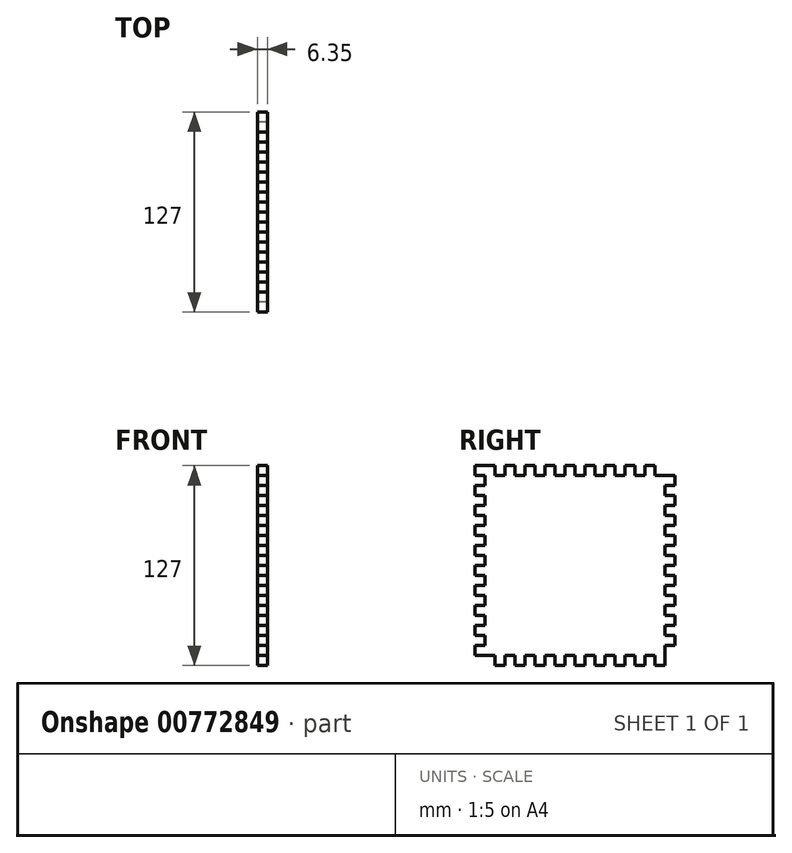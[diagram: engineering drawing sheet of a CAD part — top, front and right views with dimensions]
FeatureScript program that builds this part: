
annotation { "Feature Type Name" : "Feature", "Feature Type Description" : "" }
export const myFeature = defineFeature(function(context is Context, id is Id, definition is map)
    precondition{}
    {
        {
            var Q0;
            Q0=qCreatedBy(makeId("Right.planeOp"),FACE);
            var sketch = newSketch(context, id + "F0", { "sketchPlane" : qUnion([Q0])});
            skLineSegment(sketch, "E0.top", {"start": v(6.35, 127) * mm, "end": v(12.7, 127) * mm});
            skLineSegment(sketch, "E1.top", {"start": v(0, 120.65) * mm, "end": v(6.35, 120.65) * mm});
            skLineSegment(sketch, "E2.1.0.0", {"start": v(12.7, 127) * mm, "end": v(12.7, 120.65) * mm});
            skLineSegment(sketch, "E2.2.0.0", {"start": v(19.05, 127) * mm, "end": v(19.05, 120.65) * mm});
            skLineSegment(sketch, "E2.2.0.1", {"start": v(12.7, 120.65) * mm, "end": v(19.05, 120.65) * mm});
            skLineSegment(sketch, "E2.2.0.2", {"start": v(12.7, 127) * mm, "end": v(12.7, 120.65) * mm});
            skLineSegment(sketch, "E2.3.0.0", {"start": v(25.4, 127) * mm, "end": v(25.4, 120.65) * mm});
            skLineSegment(sketch, "E2.3.0.2", {"start": v(19.05, 127) * mm, "end": v(19.05, 120.65) * mm});
            skLineSegment(sketch, "E2.4.0.0", {"start": v(31.75, 127) * mm, "end": v(31.75, 120.65) * mm});
            skLineSegment(sketch, "E2.4.0.1", {"start": v(25.4, 120.65) * mm, "end": v(31.75, 120.65) * mm});
            skLineSegment(sketch, "E2.4.0.2", {"start": v(25.4, 127) * mm, "end": v(25.4, 120.65) * mm});
            skLineSegment(sketch, "E2.5.0.0", {"start": v(38.1, 127) * mm, "end": v(38.1, 120.65) * mm});
            skLineSegment(sketch, "E2.5.0.2", {"start": v(31.75, 127) * mm, "end": v(31.75, 120.65) * mm});
            skLineSegment(sketch, "E2.6.0.0", {"start": v(44.45, 127) * mm, "end": v(44.45, 120.65) * mm});
            skLineSegment(sketch, "E2.6.0.1", {"start": v(38.1, 120.65) * mm, "end": v(44.45, 120.65) * mm});
            skLineSegment(sketch, "E2.6.0.2", {"start": v(38.1, 127) * mm, "end": v(38.1, 120.65) * mm});
            skLineSegment(sketch, "E2.7.0.0", {"start": v(50.8, 127) * mm, "end": v(50.8, 120.65) * mm});
            skLineSegment(sketch, "E2.7.0.2", {"start": v(44.45, 127) * mm, "end": v(44.45, 120.65) * mm});
            skLineSegment(sketch, "E2.8.0.0", {"start": v(57.15, 127) * mm, "end": v(57.15, 120.65) * mm});
            skLineSegment(sketch, "E2.8.0.1", {"start": v(50.8, 120.65) * mm, "end": v(57.15, 120.65) * mm});
            skLineSegment(sketch, "E2.8.0.2", {"start": v(50.8, 127) * mm, "end": v(50.8, 120.65) * mm});
            skLineSegment(sketch, "E2.9.0.0", {"start": v(63.5, 127) * mm, "end": v(63.5, 120.65) * mm});
            skLineSegment(sketch, "E2.9.0.2", {"start": v(57.15, 127) * mm, "end": v(57.15, 120.65) * mm});
            skLineSegment(sketch, "E2.10.0.0", {"start": v(69.85, 127) * mm, "end": v(69.85, 120.65) * mm});
            skLineSegment(sketch, "E2.10.0.1", {"start": v(63.5, 120.65) * mm, "end": v(69.85, 120.65) * mm});
            skLineSegment(sketch, "E2.10.0.2", {"start": v(63.5, 127) * mm, "end": v(63.5, 120.65) * mm});
            skLineSegment(sketch, "E2.11.0.0", {"start": v(76.2, 127) * mm, "end": v(76.2, 120.65) * mm});
            skLineSegment(sketch, "E2.11.0.2", {"start": v(69.85, 127) * mm, "end": v(69.85, 120.65) * mm});
            skLineSegment(sketch, "E2.12.0.0", {"start": v(82.55, 127) * mm, "end": v(82.55, 120.65) * mm});
            skLineSegment(sketch, "E2.12.0.1", {"start": v(76.2, 120.65) * mm, "end": v(82.55, 120.65) * mm});
            skLineSegment(sketch, "E2.12.0.2", {"start": v(76.2, 127) * mm, "end": v(76.2, 120.65) * mm});
            skLineSegment(sketch, "E2.13.0.0", {"start": v(88.9, 127) * mm, "end": v(88.9, 120.65) * mm});
            skLineSegment(sketch, "E2.13.0.2", {"start": v(82.55, 127) * mm, "end": v(82.55, 120.65) * mm});
            skLineSegment(sketch, "E2.14.0.0", {"start": v(95.25, 127) * mm, "end": v(95.25, 120.65) * mm});
            skLineSegment(sketch, "E2.14.0.1", {"start": v(88.9, 120.65) * mm, "end": v(95.25, 120.65) * mm});
            skLineSegment(sketch, "E2.14.0.2", {"start": v(88.9, 127) * mm, "end": v(88.9, 120.65) * mm});
            skLineSegment(sketch, "E2.15.0.0", {"start": v(101.6, 127) * mm, "end": v(101.6, 120.65) * mm});
            skLineSegment(sketch, "E2.15.0.2", {"start": v(95.25, 127) * mm, "end": v(95.25, 120.65) * mm});
            skLineSegment(sketch, "E2.16.0.0", {"start": v(107.95, 127) * mm, "end": v(107.95, 120.65) * mm});
            skLineSegment(sketch, "E2.16.0.1", {"start": v(101.6, 120.65) * mm, "end": v(107.95, 120.65) * mm});
            skLineSegment(sketch, "E2.16.0.2", {"start": v(101.6, 127) * mm, "end": v(101.6, 120.65) * mm});
            skLineSegment(sketch, "E2.17.0.0", {"start": v(114.3, 127) * mm, "end": v(114.3, 120.65) * mm});
            skLineSegment(sketch, "E2.17.0.2", {"start": v(107.95, 127) * mm, "end": v(107.95, 120.65) * mm});
            skLineSegment(sketch, "E2.18.0.1", {"start": v(114.3, 120.65) * mm, "end": v(120.65, 120.65) * mm});
            skLineSegment(sketch, "E2.18.0.2", {"start": v(114.3, 127) * mm, "end": v(114.3, 120.65) * mm});
            skLineSegment(sketch, "E3.trimOffspring", {"start": v(19.05, 127) * mm, "end": v(25.4, 127) * mm});
            skLineSegment(sketch, "E4.trimOffspring", {"start": v(31.75, 127) * mm, "end": v(38.1, 127) * mm});
            skLineSegment(sketch, "E5.trimOffspring", {"start": v(44.45, 127) * mm, "end": v(50.8, 127) * mm});
            skLineSegment(sketch, "E6.trimOffspring", {"start": v(57.15, 127) * mm, "end": v(63.5, 127) * mm});
            skLineSegment(sketch, "E7.trimOffspring", {"start": v(69.85, 127) * mm, "end": v(76.2, 127) * mm});
            skLineSegment(sketch, "E8.trimOffspring", {"start": v(82.55, 127) * mm, "end": v(88.9, 127) * mm});
            skLineSegment(sketch, "E9.trimOffspring", {"start": v(95.25, 127) * mm, "end": v(101.6, 127) * mm});
            skLineSegment(sketch, "E10.trimOffspring", {"start": v(107.95, 127) * mm, "end": v(114.3, 127) * mm});
            skLineSegment(sketch, "E11.0.1.1", {"start": v(120.65, 114.3) * mm, "end": v(127, 114.3) * mm});
            skLineSegment(sketch, "E11.0.1.2", {"start": v(127, 120.65) * mm, "end": v(127, 114.3) * mm});
            skLineSegment(sketch, "E11.0.2.0", {"start": v(120.65, 114.3) * mm, "end": v(127, 114.3) * mm});
            skLineSegment(sketch, "E11.0.2.1", {"start": v(120.65, 107.95) * mm, "end": v(127, 107.95) * mm});
            skLineSegment(sketch, "E11.0.2.3", {"start": v(120.65, 114.3) * mm, "end": v(120.65, 107.95) * mm});
            skLineSegment(sketch, "E11.0.3.0", {"start": v(120.65, 107.95) * mm, "end": v(127, 107.95) * mm});
            skLineSegment(sketch, "E11.0.3.1", {"start": v(120.65, 101.6) * mm, "end": v(127, 101.6) * mm});
            skLineSegment(sketch, "E11.0.3.2", {"start": v(127, 107.95) * mm, "end": v(127, 101.6) * mm});
            skLineSegment(sketch, "E11.0.4.0", {"start": v(120.65, 101.6) * mm, "end": v(127, 101.6) * mm});
            skLineSegment(sketch, "E11.0.4.1", {"start": v(120.65, 95.25) * mm, "end": v(127, 95.25) * mm});
            skLineSegment(sketch, "E11.0.4.3", {"start": v(120.65, 101.6) * mm, "end": v(120.65, 95.25) * mm});
            skLineSegment(sketch, "E11.0.5.0", {"start": v(120.65, 95.25) * mm, "end": v(127, 95.25) * mm});
            skLineSegment(sketch, "E11.0.5.1", {"start": v(120.65, 88.9) * mm, "end": v(127, 88.9) * mm});
            skLineSegment(sketch, "E11.0.6.0", {"start": v(120.65, 88.9) * mm, "end": v(127, 88.9) * mm});
            skLineSegment(sketch, "E11.0.6.1", {"start": v(120.65, 82.55) * mm, "end": v(127, 82.55) * mm});
            skLineSegment(sketch, "E11.0.6.3", {"start": v(120.65, 88.9) * mm, "end": v(120.65, 82.55) * mm});
            skLineSegment(sketch, "E11.0.7.0", {"start": v(120.65, 82.55) * mm, "end": v(127, 82.55) * mm});
            skLineSegment(sketch, "E11.0.7.1", {"start": v(120.65, 76.2) * mm, "end": v(127, 76.2) * mm});
            skLineSegment(sketch, "E11.0.8.0", {"start": v(120.65, 76.2) * mm, "end": v(127, 76.2) * mm});
            skLineSegment(sketch, "E11.0.8.1", {"start": v(120.65, 69.85) * mm, "end": v(127, 69.85) * mm});
            skLineSegment(sketch, "E11.0.8.3", {"start": v(120.65, 76.2) * mm, "end": v(120.65, 69.85) * mm});
            skLineSegment(sketch, "E11.0.9.0", {"start": v(120.65, 69.85) * mm, "end": v(127, 69.85) * mm});
            skLineSegment(sketch, "E11.0.9.1", {"start": v(120.65, 63.5) * mm, "end": v(127, 63.5) * mm});
            skLineSegment(sketch, "E11.0.10.0", {"start": v(120.65, 63.5) * mm, "end": v(127, 63.5) * mm});
            skLineSegment(sketch, "E11.0.10.1", {"start": v(120.65, 57.15) * mm, "end": v(127, 57.15) * mm});
            skLineSegment(sketch, "E11.0.10.3", {"start": v(120.65, 63.5) * mm, "end": v(120.65, 57.15) * mm});
            skLineSegment(sketch, "E11.0.11.0", {"start": v(120.65, 57.15) * mm, "end": v(127, 57.15) * mm});
            skLineSegment(sketch, "E11.0.11.1", {"start": v(120.65, 50.8) * mm, "end": v(127, 50.8) * mm});
            skLineSegment(sketch, "E11.0.12.0", {"start": v(120.65, 50.8) * mm, "end": v(127, 50.8) * mm});
            skLineSegment(sketch, "E11.0.12.1", {"start": v(120.65, 44.45) * mm, "end": v(127, 44.45) * mm});
            skLineSegment(sketch, "E11.0.12.3", {"start": v(120.65, 50.8) * mm, "end": v(120.65, 44.45) * mm});
            skLineSegment(sketch, "E11.0.13.0", {"start": v(120.65, 44.45) * mm, "end": v(127, 44.45) * mm});
            skLineSegment(sketch, "E11.0.13.1", {"start": v(120.65, 38.1) * mm, "end": v(127, 38.1) * mm});
            skLineSegment(sketch, "E11.0.14.0", {"start": v(120.65, 38.1) * mm, "end": v(127, 38.1) * mm});
            skLineSegment(sketch, "E11.0.14.1", {"start": v(120.65, 31.75) * mm, "end": v(127, 31.75) * mm});
            skLineSegment(sketch, "E11.0.14.3", {"start": v(120.65, 38.1) * mm, "end": v(120.65, 31.75) * mm});
            skLineSegment(sketch, "E11.0.15.0", {"start": v(120.65, 31.75) * mm, "end": v(127, 31.75) * mm});
            skLineSegment(sketch, "E11.0.15.1", {"start": v(120.65, 25.4) * mm, "end": v(127, 25.4) * mm});
            skLineSegment(sketch, "E11.0.16.0", {"start": v(120.65, 25.4) * mm, "end": v(127, 25.4) * mm});
            skLineSegment(sketch, "E11.0.16.1", {"start": v(120.65, 19.05) * mm, "end": v(127, 19.05) * mm});
            skLineSegment(sketch, "E11.0.16.3", {"start": v(120.65, 25.4) * mm, "end": v(120.65, 19.05) * mm});
            skLineSegment(sketch, "E11.0.17.0", {"start": v(120.65, 19.05) * mm, "end": v(127, 19.05) * mm});
            skLineSegment(sketch, "E11.0.17.1", {"start": v(120.65, 12.7) * mm, "end": v(127, 12.7) * mm});
            skLineSegment(sketch, "E11.0.17.2", {"start": v(127, 19.05) * mm, "end": v(127, 12.7) * mm});
            skLineSegment(sketch, "E11.0.18.0", {"start": v(120.65, 12.7) * mm, "end": v(127, 12.7) * mm});
            skLineSegment(sketch, "E11.0.18.3", {"start": v(120.65, 12.7) * mm, "end": v(120.65, 6.35) * mm});
            skLineSegment(sketch, "E12.trimOffspring", {"start": v(127, 88.9) * mm, "end": v(127, 95.25) * mm});
            skLineSegment(sketch, "E13.trimOffspring", {"start": v(127, 76.2) * mm, "end": v(127, 82.55) * mm});
            skLineSegment(sketch, "E14.trimOffspring", {"start": v(127, 63.5) * mm, "end": v(127, 69.85) * mm});
            skLineSegment(sketch, "E15.trimOffspring", {"start": v(127, 50.8) * mm, "end": v(127, 57.15) * mm});
            skLineSegment(sketch, "E16.trimOffspring", {"start": v(127, 38.1) * mm, "end": v(127, 44.45) * mm});
            skLineSegment(sketch, "E17.trimOffspring", {"start": v(127, 25.4) * mm, "end": v(127, 31.75) * mm});
            skLineSegment(sketch, "E18.trimOffspring", {"start": v(127, 12.7) * mm, "end": v(127, 19.05) * mm});
            skLineSegment(sketch, "E19.1.0.0", {"start": v(114.3, 0) * mm, "end": v(114.3, 6.35) * mm});
            skLineSegment(sketch, "E19.1.0.3", {"start": v(114.3, 0) * mm, "end": v(120.65, 0) * mm});
            skLineSegment(sketch, "E19.2.0.0", {"start": v(107.95, 0) * mm, "end": v(107.95, 6.35) * mm});
            skLineSegment(sketch, "E19.2.0.1", {"start": v(114.3, 6.35) * mm, "end": v(107.95, 6.35) * mm});
            skLineSegment(sketch, "E19.2.0.2", {"start": v(114.3, 0) * mm, "end": v(114.3, 6.35) * mm});
            skLineSegment(sketch, "E19.3.0.0", {"start": v(101.6, 0) * mm, "end": v(101.6, 6.35) * mm});
            skLineSegment(sketch, "E19.3.0.2", {"start": v(107.95, 0) * mm, "end": v(107.95, 6.35) * mm});
            skLineSegment(sketch, "E19.3.0.3", {"start": v(101.6, 0) * mm, "end": v(107.95, 0) * mm});
            skLineSegment(sketch, "E19.4.0.0", {"start": v(95.25, 0) * mm, "end": v(95.25, 6.35) * mm});
            skLineSegment(sketch, "E19.4.0.1", {"start": v(101.6, 6.35) * mm, "end": v(95.25, 6.35) * mm});
            skLineSegment(sketch, "E19.4.0.2", {"start": v(101.6, 0) * mm, "end": v(101.6, 6.35) * mm});
            skLineSegment(sketch, "E19.5.0.0", {"start": v(88.9, 0) * mm, "end": v(88.9, 6.35) * mm});
            skLineSegment(sketch, "E19.5.0.2", {"start": v(95.25, 0) * mm, "end": v(95.25, 6.35) * mm});
            skLineSegment(sketch, "E19.5.0.3", {"start": v(88.9, 0) * mm, "end": v(95.25, 0) * mm});
            skLineSegment(sketch, "E19.6.0.0", {"start": v(82.55, 0) * mm, "end": v(82.55, 6.35) * mm});
            skLineSegment(sketch, "E19.6.0.1", {"start": v(88.9, 6.35) * mm, "end": v(82.55, 6.35) * mm});
            skLineSegment(sketch, "E19.6.0.2", {"start": v(88.9, 0) * mm, "end": v(88.9, 6.35) * mm});
            skLineSegment(sketch, "E19.7.0.0", {"start": v(76.2, 0) * mm, "end": v(76.2, 6.35) * mm});
            skLineSegment(sketch, "E19.7.0.2", {"start": v(82.55, 0) * mm, "end": v(82.55, 6.35) * mm});
            skLineSegment(sketch, "E19.7.0.3", {"start": v(76.2, 0) * mm, "end": v(82.55, 0) * mm});
            skLineSegment(sketch, "E19.8.0.0", {"start": v(69.85, 0) * mm, "end": v(69.85, 6.35) * mm});
            skLineSegment(sketch, "E19.8.0.1", {"start": v(76.2, 6.35) * mm, "end": v(69.85, 6.35) * mm});
            skLineSegment(sketch, "E19.8.0.2", {"start": v(76.2, 0) * mm, "end": v(76.2, 6.35) * mm});
            skLineSegment(sketch, "E19.9.0.0", {"start": v(63.5, 0) * mm, "end": v(63.5, 6.35) * mm});
            skLineSegment(sketch, "E19.9.0.2", {"start": v(69.85, 0) * mm, "end": v(69.85, 6.35) * mm});
            skLineSegment(sketch, "E19.9.0.3", {"start": v(63.5, 0) * mm, "end": v(69.85, 0) * mm});
            skLineSegment(sketch, "E19.10.0.0", {"start": v(57.15, 0) * mm, "end": v(57.15, 6.35) * mm});
            skLineSegment(sketch, "E19.10.0.1", {"start": v(63.5, 6.35) * mm, "end": v(57.15, 6.35) * mm});
            skLineSegment(sketch, "E19.10.0.2", {"start": v(63.5, 0) * mm, "end": v(63.5, 6.35) * mm});
            skLineSegment(sketch, "E19.11.0.0", {"start": v(50.8, 0) * mm, "end": v(50.8, 6.35) * mm});
            skLineSegment(sketch, "E19.11.0.2", {"start": v(57.15, 0) * mm, "end": v(57.15, 6.35) * mm});
            skLineSegment(sketch, "E19.11.0.3", {"start": v(50.8, 0) * mm, "end": v(57.15, 0) * mm});
            skLineSegment(sketch, "E19.12.0.0", {"start": v(44.45, 0) * mm, "end": v(44.45, 6.35) * mm});
            skLineSegment(sketch, "E19.12.0.1", {"start": v(50.8, 6.35) * mm, "end": v(44.45, 6.35) * mm});
            skLineSegment(sketch, "E19.12.0.2", {"start": v(50.8, 0) * mm, "end": v(50.8, 6.35) * mm});
            skLineSegment(sketch, "E19.13.0.0", {"start": v(38.1, 0) * mm, "end": v(38.1, 6.35) * mm});
            skLineSegment(sketch, "E19.13.0.2", {"start": v(44.45, 0) * mm, "end": v(44.45, 6.35) * mm});
            skLineSegment(sketch, "E19.13.0.3", {"start": v(38.1, 0) * mm, "end": v(44.45, 0) * mm});
            skLineSegment(sketch, "E19.14.0.0", {"start": v(31.75, 0) * mm, "end": v(31.75, 6.35) * mm});
            skLineSegment(sketch, "E19.14.0.1", {"start": v(38.1, 6.35) * mm, "end": v(31.75, 6.35) * mm});
            skLineSegment(sketch, "E19.14.0.2", {"start": v(38.1, 0) * mm, "end": v(38.1, 6.35) * mm});
            skLineSegment(sketch, "E19.15.0.0", {"start": v(25.4, 0) * mm, "end": v(25.4, 6.35) * mm});
            skLineSegment(sketch, "E19.15.0.2", {"start": v(31.75, 0) * mm, "end": v(31.75, 6.35) * mm});
            skLineSegment(sketch, "E19.15.0.3", {"start": v(25.4, 0) * mm, "end": v(31.75, 0) * mm});
            skLineSegment(sketch, "E19.16.0.0", {"start": v(19.05, 0) * mm, "end": v(19.05, 6.35) * mm});
            skLineSegment(sketch, "E19.16.0.1", {"start": v(25.4, 6.35) * mm, "end": v(19.05, 6.35) * mm});
            skLineSegment(sketch, "E19.16.0.2", {"start": v(25.4, 0) * mm, "end": v(25.4, 6.35) * mm});
            skLineSegment(sketch, "E19.17.0.0", {"start": v(12.7, 0) * mm, "end": v(12.7, 6.35) * mm});
            skLineSegment(sketch, "E19.17.0.2", {"start": v(19.05, 0) * mm, "end": v(19.05, 6.35) * mm});
            skLineSegment(sketch, "E19.17.0.3", {"start": v(12.7, 0) * mm, "end": v(19.05, 0) * mm});
            skLineSegment(sketch, "E19.18.0.1", {"start": v(12.7, 6.35) * mm, "end": v(6.35, 6.35) * mm});
            skLineSegment(sketch, "E19.18.0.2", {"start": v(12.7, 0) * mm, "end": v(12.7, 6.35) * mm});
            skLineSegment(sketch, "E19.direction1", {"start": v(120.65, 0) * mm, "end": v(114.3, 0) * mm, "construction": true});
            skLineSegment(sketch, "E20.0.1.0", {"start": v(6.35, 12.7) * mm, "end": v(0, 12.7) * mm});
            skLineSegment(sketch, "E20.0.1.1", {"start": v(0, 6.35) * mm, "end": v(0, 12.7) * mm});
            skLineSegment(sketch, "E20.0.2.0", {"start": v(6.35, 19.05) * mm, "end": v(0, 19.05) * mm});
            skLineSegment(sketch, "E20.0.2.2", {"start": v(0, 12.7) * mm, "end": v(6.35, 12.7) * mm});
            skLineSegment(sketch, "E20.0.2.3", {"start": v(6.35, 12.7) * mm, "end": v(6.35, 19.05) * mm});
            skLineSegment(sketch, "E20.0.3.0", {"start": v(6.35, 25.4) * mm, "end": v(0, 25.4) * mm});
            skLineSegment(sketch, "E20.0.3.1", {"start": v(0, 19.05) * mm, "end": v(0, 25.4) * mm});
            skLineSegment(sketch, "E20.0.3.2", {"start": v(0, 19.05) * mm, "end": v(6.35, 19.05) * mm});
            skLineSegment(sketch, "E20.0.4.0", {"start": v(6.35, 31.75) * mm, "end": v(0, 31.75) * mm});
            skLineSegment(sketch, "E20.0.4.2", {"start": v(0, 25.4) * mm, "end": v(6.35, 25.4) * mm});
            skLineSegment(sketch, "E20.0.4.3", {"start": v(6.35, 25.4) * mm, "end": v(6.35, 31.75) * mm});
            skLineSegment(sketch, "E20.0.5.0", {"start": v(6.35, 38.1) * mm, "end": v(0, 38.1) * mm});
            skLineSegment(sketch, "E20.0.5.1", {"start": v(0, 31.75) * mm, "end": v(0, 38.1) * mm});
            skLineSegment(sketch, "E20.0.5.2", {"start": v(0, 31.75) * mm, "end": v(6.35, 31.75) * mm});
            skLineSegment(sketch, "E20.0.6.0", {"start": v(6.35, 44.45) * mm, "end": v(0, 44.45) * mm});
            skLineSegment(sketch, "E20.0.6.2", {"start": v(0, 38.1) * mm, "end": v(6.35, 38.1) * mm});
            skLineSegment(sketch, "E20.0.6.3", {"start": v(6.35, 38.1) * mm, "end": v(6.35, 44.45) * mm});
            skLineSegment(sketch, "E20.0.7.0", {"start": v(6.35, 50.8) * mm, "end": v(0, 50.8) * mm});
            skLineSegment(sketch, "E20.0.7.1", {"start": v(0, 44.45) * mm, "end": v(0, 50.8) * mm});
            skLineSegment(sketch, "E20.0.7.2", {"start": v(0, 44.45) * mm, "end": v(6.35, 44.45) * mm});
            skLineSegment(sketch, "E20.0.8.0", {"start": v(6.35, 57.15) * mm, "end": v(0, 57.15) * mm});
            skLineSegment(sketch, "E20.0.8.2", {"start": v(0, 50.8) * mm, "end": v(6.35, 50.8) * mm});
            skLineSegment(sketch, "E20.0.8.3", {"start": v(6.35, 50.8) * mm, "end": v(6.35, 57.15) * mm});
            skLineSegment(sketch, "E20.0.9.0", {"start": v(6.35, 63.5) * mm, "end": v(0, 63.5) * mm});
            skLineSegment(sketch, "E20.0.9.1", {"start": v(0, 57.15) * mm, "end": v(0, 63.5) * mm});
            skLineSegment(sketch, "E20.0.9.2", {"start": v(0, 57.15) * mm, "end": v(6.35, 57.15) * mm});
            skLineSegment(sketch, "E20.0.10.0", {"start": v(6.35, 69.85) * mm, "end": v(0, 69.85) * mm});
            skLineSegment(sketch, "E20.0.10.2", {"start": v(0, 63.5) * mm, "end": v(6.35, 63.5) * mm});
            skLineSegment(sketch, "E20.0.10.3", {"start": v(6.35, 63.5) * mm, "end": v(6.35, 69.85) * mm});
            skLineSegment(sketch, "E20.0.11.0", {"start": v(6.35, 76.2) * mm, "end": v(0, 76.2) * mm});
            skLineSegment(sketch, "E20.0.11.1", {"start": v(0, 69.85) * mm, "end": v(0, 76.2) * mm});
            skLineSegment(sketch, "E20.0.11.2", {"start": v(0, 69.85) * mm, "end": v(6.35, 69.85) * mm});
            skLineSegment(sketch, "E20.0.12.0", {"start": v(6.35, 82.55) * mm, "end": v(0, 82.55) * mm});
            skLineSegment(sketch, "E20.0.12.2", {"start": v(0, 76.2) * mm, "end": v(6.35, 76.2) * mm});
            skLineSegment(sketch, "E20.0.12.3", {"start": v(6.35, 76.2) * mm, "end": v(6.35, 82.55) * mm});
            skLineSegment(sketch, "E20.0.13.0", {"start": v(6.35, 88.9) * mm, "end": v(0, 88.9) * mm});
            skLineSegment(sketch, "E20.0.13.1", {"start": v(0, 82.55) * mm, "end": v(0, 88.9) * mm});
            skLineSegment(sketch, "E20.0.13.2", {"start": v(0, 82.55) * mm, "end": v(6.35, 82.55) * mm});
            skLineSegment(sketch, "E20.0.14.0", {"start": v(6.35, 95.25) * mm, "end": v(0, 95.25) * mm});
            skLineSegment(sketch, "E20.0.14.2", {"start": v(0, 88.9) * mm, "end": v(6.35, 88.9) * mm});
            skLineSegment(sketch, "E20.0.14.3", {"start": v(6.35, 88.9) * mm, "end": v(6.35, 95.25) * mm});
            skLineSegment(sketch, "E20.0.15.0", {"start": v(6.35, 101.6) * mm, "end": v(0, 101.6) * mm});
            skLineSegment(sketch, "E20.0.15.1", {"start": v(0, 95.25) * mm, "end": v(0, 101.6) * mm});
            skLineSegment(sketch, "E20.0.15.2", {"start": v(0, 95.25) * mm, "end": v(6.35, 95.25) * mm});
            skLineSegment(sketch, "E20.0.16.0", {"start": v(6.35, 107.95) * mm, "end": v(0, 107.95) * mm});
            skLineSegment(sketch, "E20.0.16.2", {"start": v(0, 101.6) * mm, "end": v(6.35, 101.6) * mm});
            skLineSegment(sketch, "E20.0.16.3", {"start": v(6.35, 101.6) * mm, "end": v(6.35, 107.95) * mm});
            skLineSegment(sketch, "E20.0.17.0", {"start": v(6.35, 114.3) * mm, "end": v(0, 114.3) * mm});
            skLineSegment(sketch, "E20.0.17.1", {"start": v(0, 107.95) * mm, "end": v(0, 114.3) * mm});
            skLineSegment(sketch, "E20.0.17.2", {"start": v(0, 107.95) * mm, "end": v(6.35, 107.95) * mm});
            skLineSegment(sketch, "E20.0.18.0", {"start": v(6.35, 120.65) * mm, "end": v(0, 120.65) * mm});
            skLineSegment(sketch, "E20.0.18.2", {"start": v(0, 114.3) * mm, "end": v(6.35, 114.3) * mm});
            skLineSegment(sketch, "E20.0.18.3", {"start": v(6.35, 114.3) * mm, "end": v(6.35, 120.65) * mm});
            skLineSegment(sketch, "E20.0.19.0", {"start": v(6.35, 127) * mm, "end": v(0, 127) * mm});
            skLineSegment(sketch, "E20.0.19.1", {"start": v(0, 120.65) * mm, "end": v(0, 127) * mm});
            skLineSegment(sketch, "E21", {"start": v(120.65, 120.65) * mm, "end": v(127, 120.65) * mm});
            skLineSegment(sketch, "E22", {"start": v(6.35, 6.35) * mm, "end": v(0, 6.35) * mm});
            skLineSegment(sketch, "E23", {"start": v(120.65, 0) * mm, "end": v(120.65, 6.35) * mm});
            skSolve(sketch);
        }
        {
            var Q0;
            Q0=makeQuery(id+"F0.imprint","IMPRINT",FACE,{"disambiguationData":[TD([[makeQuery(id+"F0.imprint","IMPRINT",EDGE,{"derivedFrom":sQuery(id+"F0.wireOp",EDGE,"E0.bottom")}),1.0]])]});
            var Q1;
            Q1=makeQuery(id+"F0.imprint","IMPRINT",FACE,{"disambiguationData":[TD([[makeQuery(id+"F0.imprint","IMPRINT",EDGE,{"derivedFrom":sQuery(id+"F0.wireOp",EDGE,"E0.top")}),-1.0]])]});
            extrude(context, id + "F1", {"entities" : qUnion([Q0, Q1]), "depth" : 6.35 * mm, "offsetDistance" : 25.4 * mm});
        }
    });
